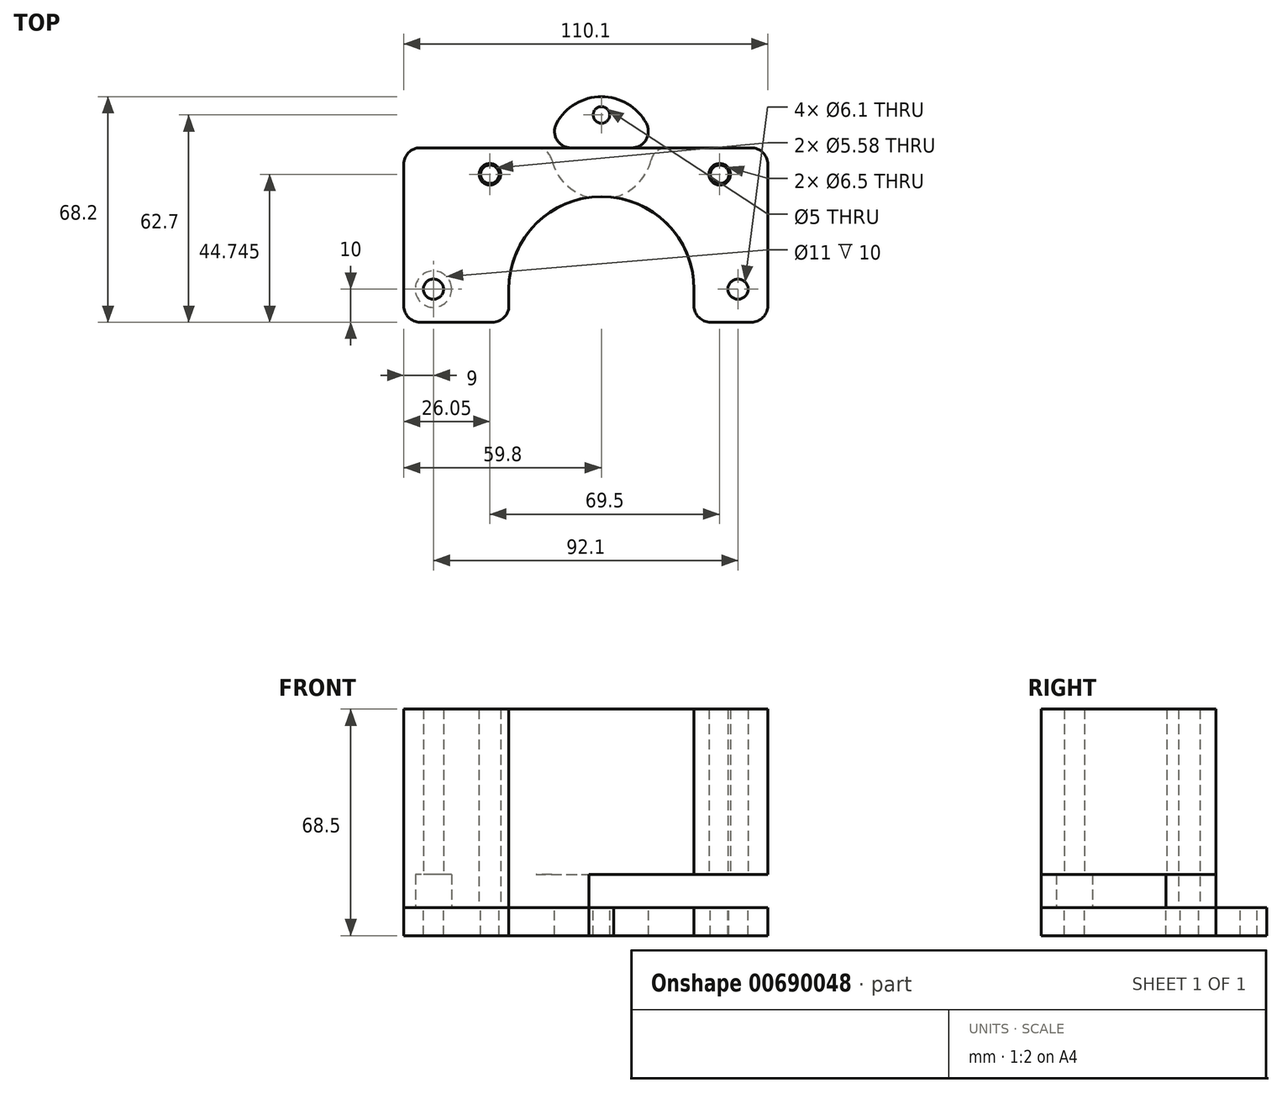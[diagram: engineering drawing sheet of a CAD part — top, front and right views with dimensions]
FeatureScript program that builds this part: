
annotation { "Feature Type Name" : "Feature", "Feature Type Description" : "" }
export const myFeature = defineFeature(function(context is Context, id is Id, definition is map)
    precondition{}
    {
        {
            var Q0;
            Q0=qCreatedBy(makeId("Top.planeOp"),FACE);
            var sketch = newSketch(context, id + "F0", { "sketchPlane" : qUnion([Q0])});
            skLineSegment(sketch, "E0.rect.bottom", {"start": v(-51, 42.93) * mm, "end": v(51, 42.93) * mm});
            skLineSegment(sketch, "E0.rect.top", {"start": v(-51, -42.93) * mm, "end": v(51, -42.93) * mm});
            skLineSegment(sketch, "E0.rect.left", {"start": v(-56, 37.92) * mm, "end": v(-56, -37.92) * mm});
            skLineSegment(sketch, "E0.rect.right", {"start": v(56, 37.92) * mm, "end": v(56, -37.92) * mm});
            skPoint(sketch, "E0.rect.middle", {"position": v(0, 0) * mm});
            skCircle(sketch, "E1", {"center": v(0, 0) * mm, "radius": 26 * mm, "construction": true});
            skCircle(sketch, "E2", {"center": v(-33.75, 34.74) * mm, "radius": 3.25 * mm});
            skCircle(sketch, "E3", {"center": v(-33.75, -34.74) * mm, "radius": 3.25 * mm});
            skCircle(sketch, "E4", {"center": v(35.75, 34.75) * mm, "radius": 3.25 * mm});
            skCircle(sketch, "E5", {"center": v(35.75, -34.74) * mm, "radius": 3.25 * mm});
            skPoint(sketch, "E6.visualSharp", {"position": v(-56, 42.93) * mm});
            skArc(sketch, "E6.filletArc", {"start": v(-51, 42.92) * mm, "mid": v(-54.54, 41.46) * mm, "end": v(-56, 37.92) * mm});
            skPoint(sketch, "E7.visualSharp", {"position": v(56, 42.92) * mm});
            skArc(sketch, "E7.filletArc", {"start": v(56, 37.92) * mm, "mid": v(54.54, 41.46) * mm, "end": v(51, 42.92) * mm});
            skPoint(sketch, "E8.visualSharp", {"position": v(56, -42.92) * mm});
            skArc(sketch, "E8.filletArc", {"start": v(51, -42.92) * mm, "mid": v(54.54, -41.46) * mm, "end": v(56, -37.92) * mm});
            skPoint(sketch, "E9.visualSharp", {"position": v(-56, -42.93) * mm});
            skArc(sketch, "E9.filletArc", {"start": v(-56, -37.92) * mm, "mid": v(-54.54, -41.46) * mm, "end": v(-51, -42.92) * mm});
            skLineSegment(sketch, "E10", {"start": v(-56, 0) * mm, "end": v(56, 0) * mm, "construction": true});
            skCircle(sketch, "E11", {"center": v(-50.8, 0) * mm, "radius": 5.5 * mm, "construction": true});
            skCircle(sketch, "E12", {"center": v(41.3, 0) * mm, "radius": 5.5 * mm, "construction": true});
            skCircle(sketch, "E13", {"center": v(0, 0) * mm, "radius": 37.5 * mm});
            skSolve(sketch);
        }
        {
            var Q0;
            Q0=makeQuery(id+"F0.imprint","IMPRINT",FACE,{"disambiguationData":[TD([[makeQuery(id+"F0.imprint","IMPRINT",EDGE,{"derivedFrom":sQuery(id+"F0.wireOp",EDGE,"E0.rect.bottom")}),-1.0]])]});
            cPlane(context, id + "F1", {"entities" : qUnion([Q0]), "cplaneType" : CPlaneType.OFFSET, "offset" : 60 * mm, "oppositeDirection" : true, "width" : 150 * mm, "height" : 150 * mm});
        }
        {
            var Q0;
            Q0=qCreatedBy(id+"F1.planeOp",FACE);
            var sketch = newSketch(context, id + "F2", { "sketchPlane" : qUnion([Q0])});
            skCircle(sketch, "E14.0", {"center": v(0, 0) * mm, "radius": 26 * mm, "construction": true});
            skCircle(sketch, "E15.0", {"center": v(-33.75, 34.74) * mm, "radius": 3.25 * mm});
            skCircle(sketch, "E16.0", {"center": v(35.75, 34.75) * mm, "radius": 3.25 * mm});
            skCircle(sketch, "E17.0", {"center": v(-50.8, 0) * mm, "radius": 5.5 * mm});
            skCircle(sketch, "E18.0", {"center": v(41.3, 0) * mm, "radius": 5.5 * mm});
            skLineSegment(sketch, "E19", {"start": v(-59.8, 0) * mm, "end": v(50.3, 0) * mm, "construction": true});
            skLineSegment(sketch, "E20", {"start": v(-59.8, 42.74) * mm, "end": v(50.3, 42.74) * mm});
            skLineSegment(sketch, "E21", {"start": v(50.3, -10) * mm, "end": v(-59.8, -10) * mm});
            skCircle(sketch, "E22.0", {"center": v(0, 0) * mm, "radius": 28 * mm});
            skCircle(sketch, "E23", {"center": v(-50.8, 0) * mm, "radius": 3.05 * mm});
            skCircle(sketch, "E24", {"center": v(41.3, 0) * mm, "radius": 3.05 * mm});
            skCircle(sketch, "E25", {"center": v(-33.75, 34.74) * mm, "radius": 2.8 * mm});
            skCircle(sketch, "E26", {"center": v(35.75, 34.75) * mm, "radius": 2.8 * mm});
            skLineSegment(sketch, "E27", {"start": v(-28, 0) * mm, "end": v(-28, -10) * mm});
            skLineSegment(sketch, "E28", {"start": v(28, 0) * mm, "end": v(28, -10) * mm});
            skCircle(sketch, "E29", {"center": v(0, 52.7) * mm, "radius": 2.5 * mm});
            skPoint(sketch, "E30.center.orphan", {"position": v(0, 42.74) * mm});
            skLineSegment(sketch, "E31", {"start": v(50.3, -10) * mm, "end": v(50.3, 42.74) * mm});
            skLineSegment(sketch, "E32", {"start": v(-59.8, 42.74) * mm, "end": v(-59.8, 42.74) * mm});
            skLineSegment(sketch, "E33", {"start": v(-59.8, -10) * mm, "end": v(-59.8, -10) * mm});
            skLineSegment(sketch, "E34", {"start": v(-59.8, 42.74) * mm, "end": v(-59.8, -10) * mm});
            skCircle(sketch, "E35", {"center": v(0, 42.74) * mm, "radius": 15.46 * mm});
            skSolve(sketch);
        }
        {
            var Q0;
            Q0=makeQuery(id+"F2.imprint","IMPRINT",FACE,{"disambiguationData":[TD([[makeQuery(id+"F2.imprint","IMPRINT",EDGE,{"derivedFrom":sQuery(id+"F2.wireOp",EDGE,"E15.0")}),-1.0]])]});
            var Q1;
            Q1=makeQuery(id+"F2.imprint","IMPRINT",FACE,{"disambiguationData":[TD([[makeQuery(id+"F2.imprint","IMPRINT",EDGE,{"derivedFrom":sQuery(id+"F2.wireOp",EDGE,"E17.0")}),1.0]])]});
            var Q2;
            Q2=makeQuery(id+"F2.imprint","IMPRINT",FACE,{"disambiguationData":[TD([[makeQuery(id+"F2.imprint","IMPRINT",EDGE,{"derivedFrom":sQuery(id+"F2.wireOp",EDGE,"E18.0")}),1.0]])]});
            var Q3;
            Q3=makeQuery(id+"F2.imprint","IMPRINT",FACE,{"disambiguationData":[TD([[makeQuery(id+"F2.imprint","IMPRINT",EDGE,{"derivedFrom":sQuery(id+"F2.wireOp",EDGE,"E15.0")}),1.0]])]});
            var Q4;
            Q4=makeQuery(id+"F2.imprint","IMPRINT",FACE,{"disambiguationData":[TD([[makeQuery(id+"F2.imprint","IMPRINT",EDGE,{"derivedFrom":sQuery(id+"F2.wireOp",EDGE,"E16.0")}),1.0]])]});
            var Q5;
            Q5=makeQuery(id+"F2.imprint","IMPRINT",FACE,{"disambiguationData":[TD([[makeQuery(id+"F2.imprint","IMPRINT",EDGE,{"derivedFrom":sQuery(id+"F2.wireOp",EDGE,"E29")}),-1.0]])]});
            var Q6;
            {var subQ0=sQuery(id+"F2.wireOp",EDGE,"E35");var subQ1=sQuery(id+"F2.wireOp",EDGE,"E20");var subQ2=makeQuery(id+"F2.imprint","INTERSECT",VERTEX,{"disambiguationData":[OD(0.0)],"derivedFrom":[subQ1,subQ0]});Q6=makeQuery(id+"F2.imprint","IMPRINT",FACE,{"disambiguationData":[TD([[makeQuery(id+"F2.imprint","IMPRINT",EDGE,{"disambiguationData":[TD([[subQ2,-1.0]])],"derivedFrom":subQ1}),-1.0]])]});}
            var Q7;
            Q7=makeQuery(id+"F2.imprint","IMPRINT",FACE,{"disambiguationData":[TD([[makeQuery(id+"F2.imprint","IMPRINT",EDGE,{"derivedFrom":sQuery(id+"F2.wireOp",EDGE,"E16.0")}),-1.0]])]});
            extrude(context, id + "F3", {"entities" : qUnion([Q0, Q1, Q2, Q3, Q4, Q5, Q6, Q7]), "oppositeDirection" : true, "depth" : 8.5 * mm, "offsetDistance" : 25 * mm});
        }
        {
            var Q0;
            Q0=makeQuery(id+"F3.opExtrude","SWEPT_EDGE",EDGE,{"disambiguationData":[OSD([sQuery(id+"F2.wireOp",EDGE,"qi17jSuA-83Sb-pjzk-zIc9-PunLo0ht189f"),sQuery(id+"F2.wireOp",EDGE,"E20")])]});
            var Q1;
            Q1=makeQuery(id+"F3.opExtrude","SWEPT_EDGE",EDGE,{"disambiguationData":[OSD([sQuery(id+"F2.wireOp",EDGE,"qi17jSuA-83Sb-pjzk-zIc9-PunLo0ht189f"),sQuery(id+"F2.wireOp",EDGE,"E21")])]});
            var Q2;
            Q2=makeQuery(id+"F3.opExtrude","SWEPT_EDGE",EDGE,{"disambiguationData":[OSD([sQuery(id+"F2.wireOp",EDGE,"E21"),sQuery(id+"F2.wireOp",EDGE,"E27")])]});
            var Q3;
            Q3=makeQuery(id+"F3.opExtrude","SWEPT_EDGE",EDGE,{"disambiguationData":[OSD([sQuery(id+"F2.wireOp",EDGE,"E21"),sQuery(id+"F2.wireOp",EDGE,"E28")])]});
            var Q4;
            Q4=makeQuery(id+"F3.opExtrude","SWEPT_EDGE",EDGE,{"disambiguationData":[OSD([sQuery(id+"F2.wireOp",EDGE,"TLaON4FH-3Sg2-Htto-DQ3E-OfpErlG6YEdG"),sQuery(id+"F2.wireOp",EDGE,"E21")])]});
            var Q5;
            Q5=makeQuery(id+"F3.opExtrude","SWEPT_EDGE",EDGE,{"disambiguationData":[OSD([sQuery(id+"F2.wireOp",EDGE,"E20"),sQuery(id+"F2.wireOp",EDGE,"TLaON4FH-3Sg2-Htto-DQ3E-OfpErlG6YEdG")])]});
            var Q6;
            {var subQ0=sQuery(id+"F2.wireOp",EDGE,"d5dd58e4-60c2-4422-8aed-d96fb367ee34.trimOffspring");var subQ1=sQuery(id+"F2.wireOp",EDGE,"E20");Q6=makeQuery(id+"F3.opExtrude","SWEPT_EDGE",EDGE,{"disambiguationData":[OSD([subQ1,subQ0]),TDD([makeQuery(id+"F2.imprint","INTERSECT",VERTEX,{"disambiguationData":[OD(1.0)],"derivedFrom":[subQ1,subQ0]})])]});}
            var Q7;
            {var subQ0=sQuery(id+"F2.wireOp",EDGE,"d5dd58e4-60c2-4422-8aed-d96fb367ee34.trimOffspring");var subQ1=sQuery(id+"F2.wireOp",EDGE,"E20");Q7=makeQuery(id+"F3.opExtrude","SWEPT_EDGE",EDGE,{"disambiguationData":[OSD([subQ1,subQ0]),TDD([makeQuery(id+"F2.imprint","INTERSECT",VERTEX,{"disambiguationData":[OD(0.0)],"derivedFrom":[subQ1,subQ0]})])]});}
            fillet(context, id + "F4", {"entities" : qUnion([Q0, Q1, Q2, Q3, Q4, Q5, Q6, Q7]), "radius" : 5 * mm, "tangentPropagation" : true, "allowEdgeOverflow" : false});
        }
        {
            var Q0;
            Q0=makeQuery(id+"F3.opExtrude","CAP_FACE",FACE,{"disambiguationData":[OSD([sQuery(id+"F2.wireOp",EDGE,"qi17jSuA-83Sb-pjzk-zIc9-PunLo0ht189f"),sQuery(id+"F2.wireOp",EDGE,"E20"),sQuery(id+"F2.wireOp",EDGE,"TLaON4FH-3Sg2-Htto-DQ3E-OfpErlG6YEdG"),sQuery(id+"F2.wireOp",EDGE,"E21"),sQuery(id+"F2.wireOp",EDGE,"E22.0"),sQuery(id+"F2.wireOp",EDGE,"E23"),sQuery(id+"F2.wireOp",EDGE,"E24"),sQuery(id+"F2.wireOp",EDGE,"E25"),sQuery(id+"F2.wireOp",EDGE,"E26"),sQuery(id+"F2.wireOp",EDGE,"E27"),sQuery(id+"F2.wireOp",EDGE,"E28")])],"isStart":true});
            var sketch = newSketch(context, id + "F5", { "sketchPlane" : qUnion([Q0])});
            skCircle(sketch, "E36.14", {"center": v(-50.8, 0) * mm, "radius": 3.05 * mm, "construction": true});
            skCircle(sketch, "E36.15", {"center": v(41.3, 0) * mm, "radius": 3.05 * mm, "construction": true});
            skCircle(sketch, "E36.16", {"center": v(35.75, 34.75) * mm, "radius": 2.8 * mm, "construction": true});
            skCircle(sketch, "E36.17", {"center": v(-33.75, 34.74) * mm, "radius": 2.8 * mm, "construction": true});
            skCircle(sketch, "E37", {"center": v(-33.75, 34.74) * mm, "radius": 3.25 * mm});
            skCircle(sketch, "E38", {"center": v(35.75, 34.75) * mm, "radius": 3.25 * mm});
            skCircle(sketch, "E39.0", {"center": v(-50.8, 0) * mm, "radius": 5.5 * mm});
            skCircle(sketch, "E40.0", {"center": v(41.3, 0) * mm, "radius": 5.5 * mm});
            skLineSegment(sketch, "E41.0.0", {"start": v(28, 0) * mm, "end": v(28, -5) * mm});
            skArc(sketch, "E41.0.1", {"start": v(28, -5) * mm, "mid": v(29.46, -8.54) * mm, "end": v(33, -10) * mm});
            skLineSegment(sketch, "E41.0.2", {"start": v(33, -10) * mm, "end": v(45.3, -10) * mm});
            skArc(sketch, "E41.0.3", {"start": v(45.3, -10) * mm, "mid": v(48.84, -8.54) * mm, "end": v(50.3, -5) * mm});
            skLineSegment(sketch, "E41.0.4", {"start": v(50.3, -5) * mm, "end": v(50.3, 37.74) * mm});
            skArc(sketch, "E41.0.5", {"start": v(50.3, 37.74) * mm, "mid": v(48.84, 41.28) * mm, "end": v(45.3, 42.74) * mm});
            skLineSegment(sketch, "E41.0.6", {"start": v(45.3, 42.74) * mm, "end": v(29.04, 42.74) * mm});
            skLineSegment(sketch, "E41.0.10", {"start": v(-25.04, 42.74) * mm, "end": v(-54.8, 42.74) * mm});
            skArc(sketch, "E41.0.11", {"start": v(-54.8, 42.74) * mm, "mid": v(-58.34, 41.28) * mm, "end": v(-59.8, 37.74) * mm});
            skLineSegment(sketch, "E41.0.12", {"start": v(-59.8, 37.74) * mm, "end": v(-59.8, -5) * mm});
            skArc(sketch, "E41.0.13", {"start": v(-59.8, -5) * mm, "mid": v(-58.34, -8.54) * mm, "end": v(-54.8, -10) * mm});
            skLineSegment(sketch, "E41.0.14", {"start": v(-54.8, -10) * mm, "end": v(-33, -10) * mm});
            skArc(sketch, "E41.0.15", {"start": v(-33, -10) * mm, "mid": v(-29.46, -8.54) * mm, "end": v(-28, -5) * mm});
            skLineSegment(sketch, "E41.0.16", {"start": v(-28, -5) * mm, "end": v(-28, 0) * mm});
            skArc(sketch, "E41.0.17", {"start": v(-28, 0) * mm, "mid": v(0, 28) * mm, "end": v(28, 0) * mm});
            skLineSegment(sketch, "E42", {"start": v(-25.04, 42.75) * mm, "end": v(29.04, 42.75) * mm});
            skSolve(sketch);
        }
        {
            var Q0;
            Q0=makeQuery(id+"F5.imprint","IMPRINT",FACE,{"disambiguationData":[TD([[makeQuery(id+"F5.imprint","IMPRINT",EDGE,{"derivedFrom":sQuery(id+"F5.wireOp",EDGE,"E37")}),-1.0]])]});
            extrude(context, id + "F6", {"entities" : qUnion([Q0]), "depth" : 10 * mm, "offsetDistance" : 25 * mm});
        }
        {
            var Q0;
            Q0=makeQuery(id+"F6.opExtrude","CAP_FACE",FACE,{"disambiguationData":[OSD([sQuery(id+"F5.wireOp",EDGE,"59007973-fc9b-4d73-a95b-948ffdd74a4d.0"),sQuery(id+"F5.wireOp",EDGE,"E36.0"),sQuery(id+"F5.wireOp",EDGE,"E36.2"),sQuery(id+"F5.wireOp",EDGE,"E36.3"),sQuery(id+"F5.wireOp",EDGE,"E36.4"),sQuery(id+"F5.wireOp",EDGE,"E36.5"),sQuery(id+"F5.wireOp",EDGE,"E36.6"),sQuery(id+"F5.wireOp",EDGE,"E36.7"),sQuery(id+"F5.wireOp",EDGE,"E36.8"),sQuery(id+"F5.wireOp",EDGE,"E36.9"),sQuery(id+"F5.wireOp",EDGE,"E36.10"),sQuery(id+"F5.wireOp",EDGE,"E36.11"),sQuery(id+"F5.wireOp",EDGE,"E36.12"),sQuery(id+"F5.wireOp",EDGE,"E36.13"),sQuery(id+"F5.wireOp",EDGE,"E37"),sQuery(id+"F5.wireOp",EDGE,"E38"),sQuery(id+"F5.wireOp",EDGE,"E39.0"),sQuery(id+"F5.wireOp",EDGE,"E40.0")])],"isStart":false});
            var sketch = newSketch(context, id + "F7", { "sketchPlane" : qUnion([Q0])});
            skArc(sketch, "E43.0.0", {"start": v(-28, 0) * mm, "mid": v(0, 28) * mm, "end": v(28, 0) * mm});
            skLineSegment(sketch, "E43.0.1", {"start": v(28, 0) * mm, "end": v(28, -5) * mm});
            skArc(sketch, "E43.0.2", {"start": v(28, -5) * mm, "mid": v(29.46, -8.54) * mm, "end": v(33, -10) * mm});
            skLineSegment(sketch, "E43.0.3", {"start": v(33, -10) * mm, "end": v(45.3, -10) * mm});
            skArc(sketch, "E43.0.4", {"start": v(45.3, -10) * mm, "mid": v(48.84, -8.54) * mm, "end": v(50.3, -5) * mm});
            skLineSegment(sketch, "E43.0.5", {"start": v(50.3, -5) * mm, "end": v(50.3, 37.74) * mm});
            skArc(sketch, "E43.0.6", {"start": v(50.3, 37.74) * mm, "mid": v(48.84, 41.28) * mm, "end": v(45.3, 42.74) * mm});
            skLineSegment(sketch, "E43.0.7", {"start": v(45.3, 42.75) * mm, "end": v(45.3, 42.75) * mm});
            skArc(sketch, "E43.0.12", {"start": v(-54.8, 42.74) * mm, "mid": v(-58.34, 41.28) * mm, "end": v(-59.8, 37.74) * mm});
            skLineSegment(sketch, "E43.0.13", {"start": v(-59.8, 37.74) * mm, "end": v(-59.8, -5) * mm});
            skArc(sketch, "E43.0.14", {"start": v(-59.8, -5) * mm, "mid": v(-58.34, -8.54) * mm, "end": v(-54.8, -10) * mm});
            skLineSegment(sketch, "E43.0.15", {"start": v(-54.8, -10) * mm, "end": v(-33, -10) * mm});
            skArc(sketch, "E43.0.16", {"start": v(-33, -10) * mm, "mid": v(-29.46, -8.54) * mm, "end": v(-28, -5) * mm});
            skLineSegment(sketch, "E43.0.17", {"start": v(-28, -5) * mm, "end": v(-28, 0) * mm});
            skCircle(sketch, "E44.0", {"center": v(-50.8, 0) * mm, "radius": 3.05 * mm});
            skCircle(sketch, "E45.0", {"center": v(-33.75, 34.74) * mm, "radius": 3.25 * mm});
            skCircle(sketch, "E46.0", {"center": v(35.75, 34.75) * mm, "radius": 3.25 * mm});
            skCircle(sketch, "E47.0", {"center": v(41.3, 0) * mm, "radius": 3.05 * mm});
            skLineSegment(sketch, "E48", {"start": v(-54.8, 42.75) * mm, "end": v(45.3, 42.75) * mm});
            skSolve(sketch);
        }
        {
            var Q0;
            Q0=makeQuery(id+"F7.imprint","IMPRINT",FACE,{"disambiguationData":[TD([[makeQuery(id+"F7.imprint","IMPRINT",EDGE,{"derivedFrom":makeQuery(id+"F6.opExtrude","CAP_EDGE",EDGE,{"disambiguationData":[OSD([sQuery(id+"F5.wireOp",EDGE,"E39.0")])],"isStart":false})}),1.0]])]});
            var Q1;
            Q1=makeQuery(id+"F7.imprint","IMPRINT",FACE,{"disambiguationData":[TD([[makeQuery(id+"F7.imprint","IMPRINT",EDGE,{"derivedFrom":makeQuery(id+"F6.opExtrude","CAP_EDGE",EDGE,{"disambiguationData":[OSD([sQuery(id+"F5.wireOp",EDGE,"E40.0")])],"isStart":false})}),1.0]])]});
            var Q2;
            Q2=makeQuery(id+"F7.imprint","IMPRINT",FACE,{"disambiguationData":[TD([[makeQuery(id+"F7.imprint","IMPRINT",EDGE,{"derivedFrom":sQuery(id+"F7.wireOp",EDGE,"eafc4506-5cf3-4060-a003-5ad796ca4b1e.0.0")}),-1.0]])]});
            var Q3;
            Q3=makeQuery(id+"F7.imprint","IMPRINT",FACE,{"disambiguationData":[TD([[makeQuery(id+"F7.imprint","IMPRINT",EDGE,{"derivedFrom":sQuery(id+"F7.wireOp",EDGE,"E43.0.0")}),-1.0]])]});
            extrude(context, id + "F8", {"entities" : qUnion([Q0, Q1, Q2, Q3]), "operationType" : NewBodyOperationType.ADD, "depth" : 50 * mm, "offsetDistance" : 25 * mm});
        }
    });
